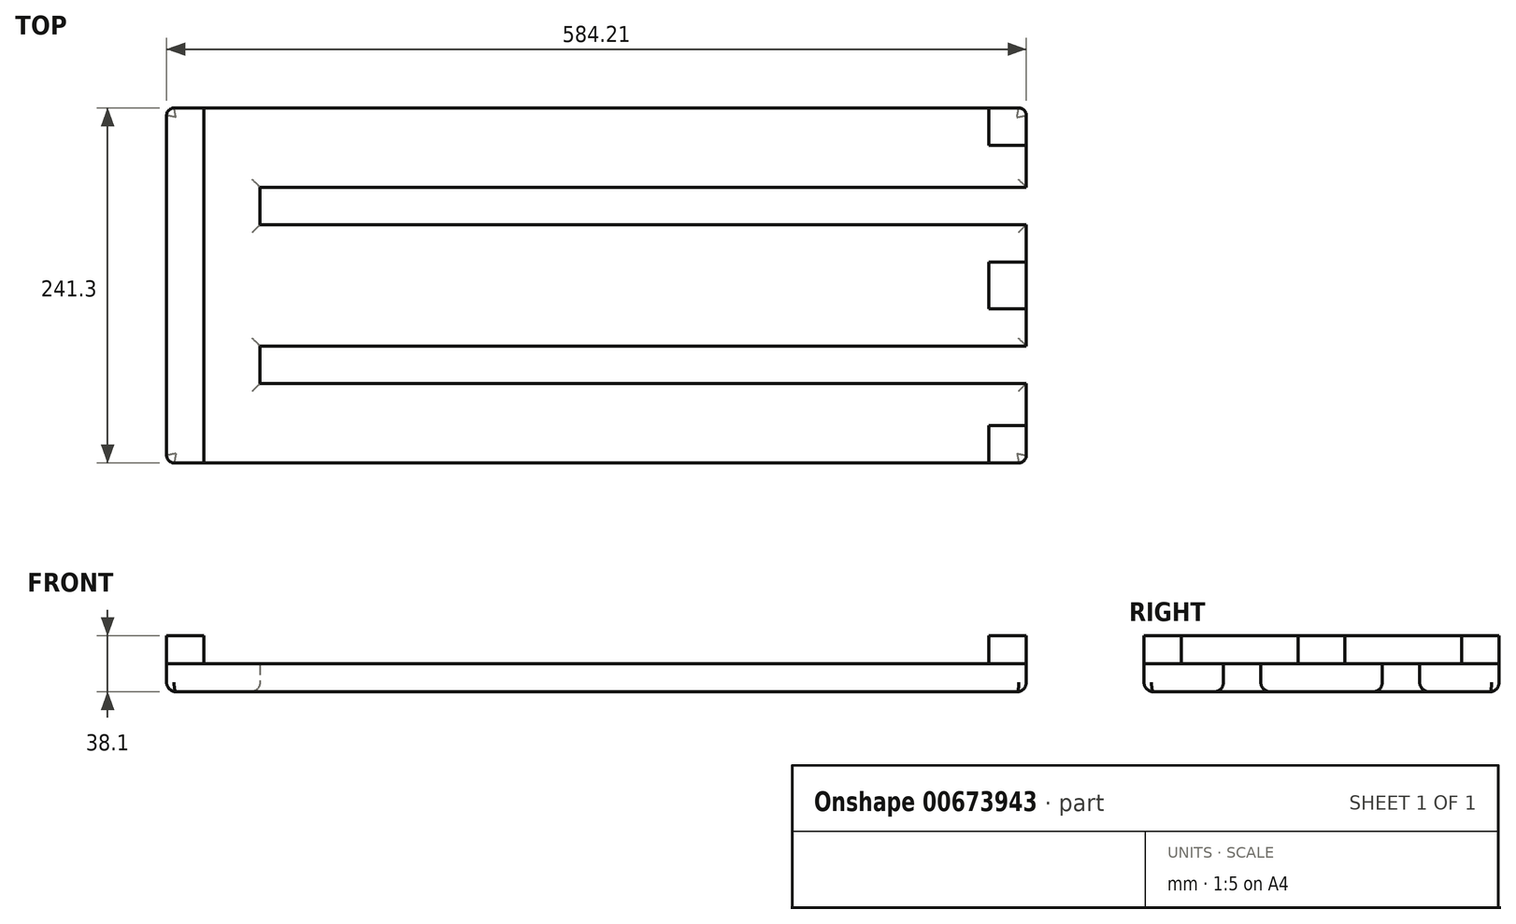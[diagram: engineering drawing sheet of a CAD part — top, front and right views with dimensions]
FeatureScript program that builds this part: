
annotation { "Feature Type Name" : "Feature", "Feature Type Description" : "" }
export const myFeature = defineFeature(function(context is Context, id is Id, definition is map)
    precondition{}
    {
        {
            var Q0;
            Q0=qCreatedBy(makeId("Top.planeOp"),FACE);
            var sketch = newSketch(context, id + "F0", { "sketchPlane" : qUnion([Q0])});
            skLineSegment(sketch, "E0.bottom", {"start": v(250.83, -120.65) * mm, "end": v(-333.38, -120.65) * mm});
            skPoint(sketch, "E0.middle", {"position": v(0, 0) * mm});
            skCircle(sketch, "E1", {"center": v(-266.7, 53.98) * mm, "radius": 41.28 * mm, "construction": true});
            skCircle(sketch, "E2", {"center": v(-180.97, 53.98) * mm, "radius": 41.28 * mm, "construction": true});
            skCircle(sketch, "E3", {"center": v(-95.25, 53.98) * mm, "radius": 41.28 * mm, "construction": true});
            skCircle(sketch, "E4", {"center": v(-9.52, 53.98) * mm, "radius": 41.28 * mm, "construction": true});
            skCircle(sketch, "E5", {"center": v(76.2, 53.98) * mm, "radius": 41.28 * mm, "construction": true});
            skCircle(sketch, "E6", {"center": v(161.93, 53.98) * mm, "radius": 41.28 * mm, "construction": true});
            skLineSegment(sketch, "E7", {"start": v(-307.98, 53.98) * mm, "end": v(285.75, 53.98) * mm, "construction": true});
            skLineSegment(sketch, "E8", {"start": v(-269.88, 66.67) * mm, "end": v(-269.88, 41.27) * mm});
            skLineSegment(sketch, "E9", {"start": v(-333.38, 120.65) * mm, "end": v(-333.38, -120.65) * mm});
            skLineSegment(sketch, "E10.trimOffspring", {"start": v(-269.88, 66.67) * mm, "end": v(250.83, 66.68) * mm});
            skLineSegment(sketch, "E11.trimOffspring", {"start": v(-269.88, 41.27) * mm, "end": v(250.83, 41.28) * mm});
            skLineSegment(sketch, "E12", {"start": v(-333.38, 120.65) * mm, "end": v(250.83, 120.65) * mm});
            skLineSegment(sketch, "E13", {"start": v(250.83, 120.65) * mm, "end": v(250.83, 66.68) * mm});
            skLineSegment(sketch, "E14.trimOffspring", {"start": v(250.83, 41.28) * mm, "end": v(250.83, -41.28) * mm});
            skLineSegment(sketch, "E15.MirrorCS", {"start": v(-269.88, -66.67) * mm, "end": v(-269.88, -41.27) * mm});
            skCircle(sketch, "E16.MirrorC", {"center": v(76.2, -53.98) * mm, "radius": 41.28 * mm, "construction": true});
            skCircle(sketch, "E17.MirrorC", {"center": v(-9.52, -53.98) * mm, "radius": 41.28 * mm, "construction": true});
            skCircle(sketch, "E18.MirrorC", {"center": v(161.93, -53.98) * mm, "radius": 41.28 * mm, "construction": true});
            skLineSegment(sketch, "E19.MirrorCS", {"start": v(-269.88, -41.27) * mm, "end": v(250.83, -41.28) * mm});
            skCircle(sketch, "E20.MirrorC", {"center": v(-266.7, -53.98) * mm, "radius": 41.28 * mm, "construction": true});
            skCircle(sketch, "E21.MirrorC", {"center": v(-180.97, -53.98) * mm, "radius": 41.28 * mm, "construction": true});
            skCircle(sketch, "E22.MirrorC", {"center": v(-95.25, -53.98) * mm, "radius": 41.28 * mm, "construction": true});
            skLineSegment(sketch, "E23.MirrorCS", {"start": v(-269.88, -66.67) * mm, "end": v(250.83, -66.68) * mm});
            skLineSegment(sketch, "E24.trimOffspring", {"start": v(250.83, -66.68) * mm, "end": v(250.83, -120.65) * mm});
            skSolve(sketch);
        }
        {
            var Q0;
            Q0=makeQuery(id+"F0.imprint","IMPRINT",FACE,{"disambiguationData":[TD([[makeQuery(id+"F0.imprint","IMPRINT",EDGE,{"derivedFrom":sQuery(id+"F0.wireOp",EDGE,"E0.bottom")}),-1.0]])]});
            extrude(context, id + "F1", {"entities" : qUnion([Q0]), "depth" : 19.05 * mm, "offsetDistance" : 25.4 * mm});
        }
        {
            var Q0;
            Q0=makeQuery(id+"F1.opExtrude","CAP_FACE",FACE,{"disambiguationData":[OSD([sQuery(id+"F0.wireOp",EDGE,"E0.bottom"),sQuery(id+"F0.wireOp",EDGE,"E8"),sQuery(id+"F0.wireOp",EDGE,"E9"),sQuery(id+"F0.wireOp",EDGE,"E10.trimOffspring"),sQuery(id+"F0.wireOp",EDGE,"E11.trimOffspring"),sQuery(id+"F0.wireOp",EDGE,"E12"),sQuery(id+"F0.wireOp",EDGE,"E13"),sQuery(id+"F0.wireOp",EDGE,"E14.trimOffspring"),sQuery(id+"F0.wireOp",EDGE,"E15.MirrorCS"),sQuery(id+"F0.wireOp",EDGE,"E19.MirrorCS"),sQuery(id+"F0.wireOp",EDGE,"E23.MirrorCS"),sQuery(id+"F0.wireOp",EDGE,"E24.trimOffspring")])],"isStart":false});
            var sketch = newSketch(context, id + "F2", { "sketchPlane" : qUnion([Q0])});
            skLineSegment(sketch, "E25.0", {"start": v(-333.38, 120.65) * mm, "end": v(-333.38, -120.65) * mm});
            skLineSegment(sketch, "E26.0", {"start": v(-307.98, 120.65) * mm, "end": v(-307.98, -120.65) * mm});
            skLineSegment(sketch, "E27.0", {"start": v(-333.38, 120.65) * mm, "end": v(-307.98, 120.65) * mm});
            skLineSegment(sketch, "E28.0", {"start": v(-307.97, -120.65) * mm, "end": v(-333.38, -120.65) * mm});
            skPoint(sketch, "E29.orphan", {"position": v(250.83, 120.65) * mm});
            skPoint(sketch, "E30.orphan", {"position": v(250.83, -120.65) * mm});
            skLineSegment(sketch, "E31.0", {"start": v(250.83, 120.65) * mm, "end": v(250.83, 95.25) * mm});
            skLineSegment(sketch, "E32.0", {"start": v(250.83, 15.88) * mm, "end": v(250.83, -15.88) * mm});
            skLineSegment(sketch, "E33.0", {"start": v(250.83, -95.25) * mm, "end": v(250.83, -120.65) * mm});
            skLineSegment(sketch, "E34.0", {"start": v(225.43, 120.65) * mm, "end": v(225.43, 95.25) * mm});
            skLineSegment(sketch, "E35.0", {"start": v(225.43, 15.88) * mm, "end": v(225.43, -15.88) * mm});
            skLineSegment(sketch, "E36.0", {"start": v(225.43, -95.25) * mm, "end": v(225.43, -120.65) * mm});
            skLineSegment(sketch, "E37.0", {"start": v(250.83, -120.65) * mm, "end": v(225.43, -120.65) * mm});
            skPoint(sketch, "E38.orphan", {"position": v(-269.88, -66.67) * mm});
            skPoint(sketch, "E39.orphan", {"position": v(-269.88, -41.27) * mm});
            skPoint(sketch, "E40.orphan", {"position": v(-269.88, 41.27) * mm});
            skLineSegment(sketch, "E41.trimOffspring", {"start": v(225.42, 120.65) * mm, "end": v(250.83, 120.65) * mm});
            skPoint(sketch, "E42.orphan", {"position": v(-269.88, 66.67) * mm});
            skLineSegment(sketch, "E43.0", {"start": v(250.83, -95.25) * mm, "end": v(225.43, -95.25) * mm});
            skPoint(sketch, "E44.orphan", {"position": v(250.83, -66.68) * mm});
            skLineSegment(sketch, "E45.0", {"start": v(225.43, -15.88) * mm, "end": v(250.83, -15.88) * mm});
            skLineSegment(sketch, "E46.0", {"start": v(225.43, 15.88) * mm, "end": v(250.83, 15.88) * mm});
            skPoint(sketch, "E47.0.end.orphan", {"position": v(250.83, 66.68) * mm});
            skPoint(sketch, "E48.orphan", {"position": v(250.83, 41.28) * mm});
            skPoint(sketch, "E49.orphan", {"position": v(250.83, -41.28) * mm});
            skLineSegment(sketch, "E50.0", {"start": v(225.42, 95.25) * mm, "end": v(250.83, 95.25) * mm});
            skSolve(sketch);
        }
        {
            var Q0;
            Q0 = qSketchRegion(id + "F2", true);
            extrude(context, id + "F3", {"entities" : qUnion([Q0]), "depth" : 19.05 * mm, "offsetDistance" : 25.4 * mm});
        }
        {
            var Q0;
            Q0=makeQuery(id+"F1.opExtrude","CAP_EDGE",EDGE,{"disambiguationData":[OSD([sQuery(id+"F0.wireOp",EDGE,"E0.bottom")])],"isStart":true});
            var Q1;
            Q1=makeQuery(id+"F1.opExtrude","CAP_FACE",FACE,{"disambiguationData":[OSD([sQuery(id+"F0.wireOp",EDGE,"E0.bottom"),sQuery(id+"F0.wireOp",EDGE,"E8"),sQuery(id+"F0.wireOp",EDGE,"E9"),sQuery(id+"F0.wireOp",EDGE,"E10.trimOffspring"),sQuery(id+"F0.wireOp",EDGE,"E11.trimOffspring"),sQuery(id+"F0.wireOp",EDGE,"E12"),sQuery(id+"F0.wireOp",EDGE,"E13"),sQuery(id+"F0.wireOp",EDGE,"E14.trimOffspring"),sQuery(id+"F0.wireOp",EDGE,"E15.MirrorCS"),sQuery(id+"F0.wireOp",EDGE,"E19.MirrorCS"),sQuery(id+"F0.wireOp",EDGE,"E23.MirrorCS"),sQuery(id+"F0.wireOp",EDGE,"E24.trimOffspring")])],"isStart":true});
            fillet(context, id + "F4", {"entities" : qUnion([Q0, Q1]), "radius" : 6.35 * mm, "tangentPropagation" : true, "allowEdgeOverflow" : false});
        }
        {
            var Q0;
            Q0=makeQuery(id+"F3.opExtrude","SWEPT_EDGE",EDGE,{"disambiguationData":[OSD([sQuery(id+"F2.wireOp",EDGE,"E25.0"),sQuery(id+"F2.wireOp",EDGE,"E27.0")])]});
            fillet(context, id + "F5", {"entities" : qUnion([Q0]), "radius" : 5.08 * mm, "tangentPropagation" : true, "allowEdgeOverflow" : false});
        }
        {
            var Q0;
            Q0=makeQuery(id+"F1.opExtrude","SWEPT_EDGE",EDGE,{"disambiguationData":[OSD([sQuery(id+"F0.wireOp",EDGE,"E9"),sQuery(id+"F0.wireOp",EDGE,"E12")])]});
            var Q1;
            Q1=makeQuery(id+"F3.opExtrude","SWEPT_EDGE",EDGE,{"disambiguationData":[OSD([sQuery(id+"F2.wireOp",EDGE,"E25.0"),sQuery(id+"F2.wireOp",EDGE,"E28.0")])]});
            var Q2;
            Q2=makeQuery(id+"F1.opExtrude","SWEPT_EDGE",EDGE,{"disambiguationData":[OSD([sQuery(id+"F0.wireOp",EDGE,"E0.bottom"),sQuery(id+"F0.wireOp",EDGE,"E9")])]});
            var Q3;
            Q3=makeQuery(id+"F1.opExtrude","SWEPT_EDGE",EDGE,{"disambiguationData":[OSD([sQuery(id+"F0.wireOp",EDGE,"E0.bottom"),sQuery(id+"F0.wireOp",EDGE,"E24.trimOffspring")])]});
            var Q4;
            Q4=makeQuery(id+"F1.opExtrude","SWEPT_EDGE",EDGE,{"disambiguationData":[OSD([sQuery(id+"F0.wireOp",EDGE,"E12"),sQuery(id+"F0.wireOp",EDGE,"E13")])]});
            var Q5;
            Q5=makeQuery(id+"F3.opExtrude","SWEPT_EDGE",EDGE,{"disambiguationData":[OSD([sQuery(id+"F2.wireOp",EDGE,"E31.0"),sQuery(id+"F2.wireOp",EDGE,"E41.trimOffspring")])]});
            fillet(context, id + "F6", {"entities" : qUnion([Q0, Q1, Q2, Q3, Q4, Q5]), "radius" : 5.08 * mm, "tangentPropagation" : true, "allowEdgeOverflow" : false});
        }
        {
            var Q0;
            Q0=makeQuery(id+"F3.opExtrude","SWEPT_EDGE",EDGE,{"disambiguationData":[OSD([sQuery(id+"F2.wireOp",EDGE,"E33.0"),sQuery(id+"F2.wireOp",EDGE,"E37.0")])]});
            fillet(context, id + "F7", {"entities" : qUnion([Q0]), "radius" : 5.08 * mm, "tangentPropagation" : true, "allowEdgeOverflow" : false});
        }
    });
